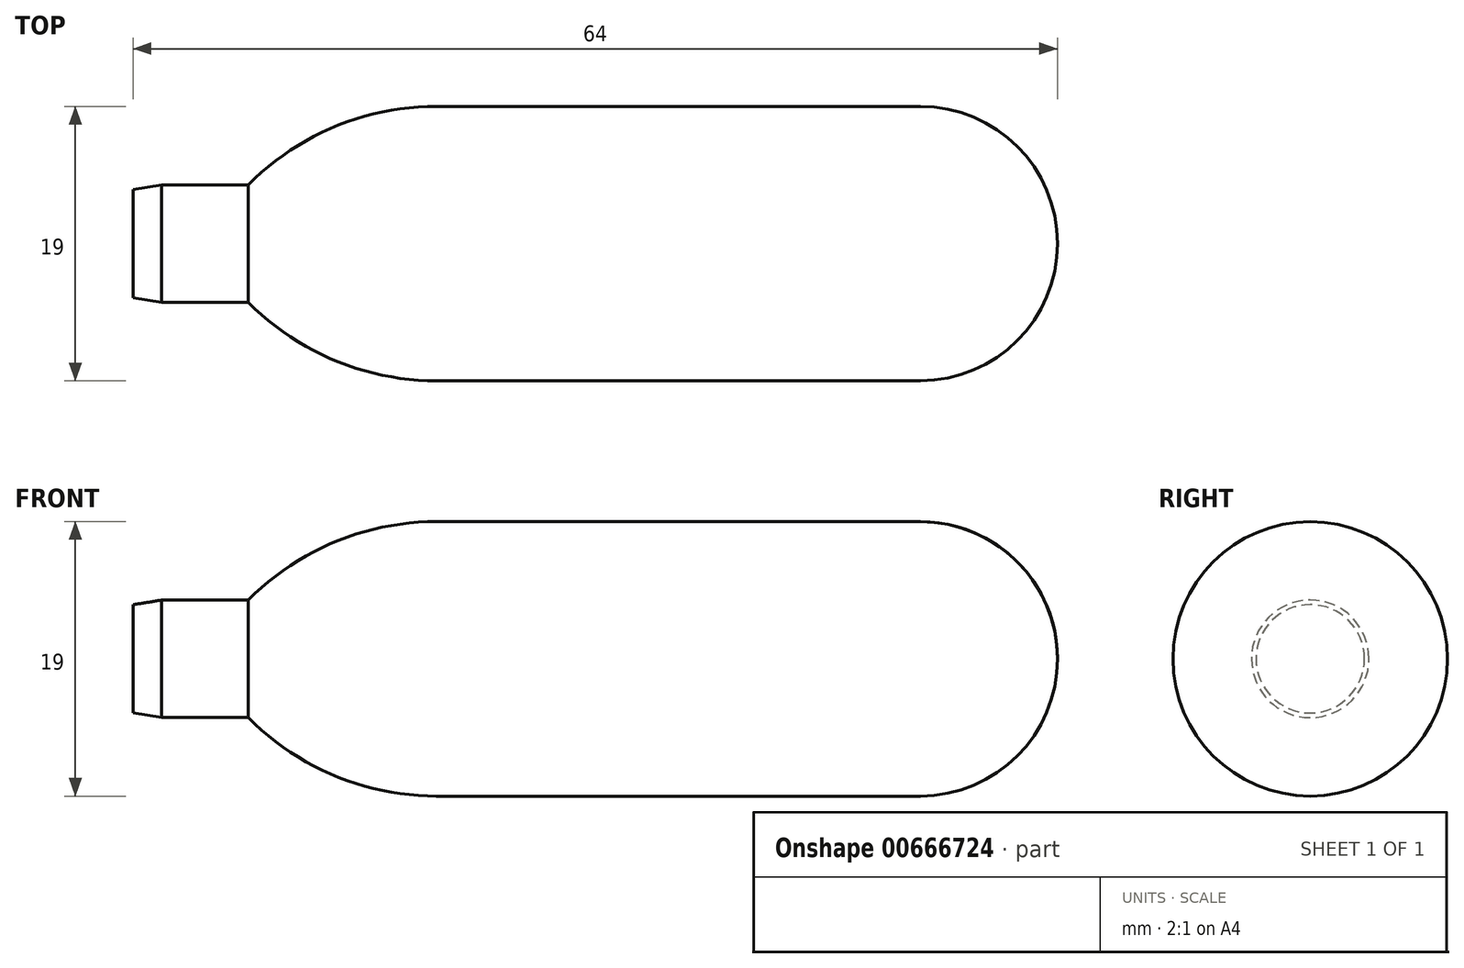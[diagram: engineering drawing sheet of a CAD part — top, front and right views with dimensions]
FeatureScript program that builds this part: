
annotation { "Feature Type Name" : "Feature", "Feature Type Description" : "" }
export const myFeature = defineFeature(function(context is Context, id is Id, definition is map)
    precondition{}
    {
        {
            var Q0;
            Q0=qCreatedBy(makeId("Front.planeOp"),FACE);
            var sketch = newSketch(context, id + "F0", { "sketchPlane" : qUnion([Q0])});
            skLineSegment(sketch, "E0", {"start": v(0, 0) * mm, "end": v(64, 0) * mm});
            skLineSegment(sketch, "E1", {"start": v(54.5, 9.5) * mm, "end": v(21, 9.5) * mm});
            skLineSegment(sketch, "E2", {"start": v(0, 0) * mm, "end": v(0, 3.75) * mm});
            skLineSegment(sketch, "E3", {"start": v(0, 3.75) * mm, "end": v(1.97, 4.07) * mm});
            skLineSegment(sketch, "E4", {"start": v(1.97, 4.07) * mm, "end": v(7.97, 4.07) * mm});
            skArc(sketch, "E5", {"start": v(21, 9.5) * mm, "mid": v(13.94, 8.09) * mm, "end": v(7.97, 4.07) * mm});
            skArc(sketch, "E6", {"start": v(64, 0) * mm, "mid": v(61.22, 6.72) * mm, "end": v(54.5, 9.5) * mm});
            skSolve(sketch);
        }
        {
            var Q0;
            Q0=makeQuery(id+"F0.imprint","IMPRINT",FACE,{"disambiguationData":[TD([[makeQuery(id+"F0.imprint","IMPRINT",EDGE,{"derivedFrom":sQuery(id+"F0.wireOp",EDGE,"E0")}),1.0]])]});
            var Q1;
            Q1=sQuery(id+"F0.wireOp",EDGE,"E0");
            revolve(context, id + "F1", {"entities" : qUnion([Q0]), "axis" : qUnion([Q1]), "revolveType" : RevolveType.FULL});
        }
    });
